# Revit family: VNRZ - 5.125'' 2-5-Door - All
name_source: partatom
category: Mechanical Equipment
units: mm (PartAtom-declared; Revit-internal decimal feet)

## family parameters
Always vertical = Yes
Cut with Voids When Loaded = No
OmniClass Number = 23.40.40.11.17
OmniClass Title = Refrigerated Cases
Part Type = Normal
Room Calculation Point = No
Round Connector Dimension = Use Diameter
Shared = Yes
Work Plane-Based = Yes

## types (5) — shared parameters
24" Shelf = Yes
DATE = 03-16-2015
DEFROST WATTAGE = 0 W
DESIGNERS NAME = SHIDDRAMESH
DISCHARGE AIR TEMP = 0 °F
Default Elevation = 48"
Defrosts Per Day_2 = 1
Description = VNRZ
Discharge Air Velocity (FPM) = 455
END PANEL = <By Category>
EQUIPMENT DESCRIPTION = VNRZ
EQUIPMENT MARK = VNRZ
Electric Defrost Fail-Safe = 46
Electric Defrost Termination Temp (°F) = 50
GLASS = Glass
GLASS CLAMP = <By Category>
Heated/Low E = Heated
Height = 83 7/8"
Hot Gas Defrost Fail-Safe = 24
Hot Gas Defrost Termination = 73° F
Item Description = VNRZ
Keynote = VNRZ
Legend Number = VNRZ
Manufacturer = HILL PHOENIX
Model = VNRZ
PAINTED METAL UPPER SHELF = <By Category>
PVC PIPE = <By Category>
Run-Off Time (Min) = 13 - 15
STAINLESS STEEL = GALVANIZED STEEL
Size of Door = 30"
Superheat Set Point @ Bulb (°F) = 3-5
URL = http://www.hillphoenix.com
Width = 37 1/8"
zero-valued in all types: Actual Weight, Load Mbh

## per-type parameters (varying)
- 2-Door - Frozen - Heated: Application Discipline=Frozen; BTUH Conventional=1091; BTUH Parallel=1071; CENTER LINE=30"; Combined Heated Rails Amps=1 A; Combined Heated Rails Watts=72 W; Combined Low E Rails Amps=0 A; Combined Low E Rails Watts=43 W; DOOR CONFIGURATION=MASTER DOOR : 30" X 75" 2 DOOR A SWING (LEFT OPENING); DRAIN HEATER AMPS=1 A; DRAIN HEATER WATTS=152 W; Defrost (Phase 1) 208 V Amps=7 A; Defrost (Phase 1) 208 V Watts=1552 W; Defrost (Phase 1) 240 V Amps=9 A; Defrost (Phase 1) 240 V Watts=2068 W; Discharge Air (°F)=-1; Eliminaator Amps=3 A; Eliminaator Watts=312 W; Evaporator (°F)=-7; GE Immersion Amps=0 A; GE Immersion Watts=37 W; High Efficiency Amps=1 A; High Efficiency Watts=52 W; Individual 101-LE Frame Amps=1 A; Individual 101-LE Frame Watts=163 W; Individual Heated Doors Amps=1 A; Individual Heated Doors Watts=79 W; Individual Low E Doors Amps=0 A; Individual Low E Doors Watts=45 W; Length=60"; Length of Cases=60"; No. OF DOORS=2; Number of Fans=2; Optimax Pro Amps=0 A; Optimax Pro Watts=43 W; REF PLANE LEFT RIGHT=30"; REFRIGERATION PIPING=COPPER PIPE; Tank/Drain Heater Amps=1 A; Tank/Drain Heater Watts=152 W; Trim colour=Render Material 255-255-255; Type of Door Swing=B-Swing; pannel colour=Render Material 255-127-0
- 3-Door - Frozen - Heated: Application Discipline=Frozen; BTUH Conventional=1037; BTUH Parallel=1017; CENTER LINE=45"; Combined Heated Rails Amps=1 A; Combined Heated Rails Watts=109 W; Combined Low E Rails Amps=1 A; Combined Low E Rails Watts=64 W; DOOR CONFIGURATION=MASTER DOOR : 30" X 75" 3 DOOR A SWING (LEFT OPENING); DRAIN HEATER AMPS=1 A; DRAIN HEATER WATTS=171 W; Defrost (Phase 1) 208 V Amps=11 A; Defrost (Phase 1) 208 V Watts=2274 W; Defrost (Phase 1) 240 V Amps=13 A; Defrost (Phase 1) 240 V Watts=3018 W; Discharge Air (°F)=-1; Eliminaator Amps=4 A; Eliminaator Watts=461 W; Evaporator (°F)=-7; GE Immersion Amps=0 A; GE Immersion Watts=55 W; High Efficiency Amps=1 A; High Efficiency Watts=78 W; Individual 101-LE Frame Amps=2 A; Individual 101-LE Frame Watts=228 W; Individual Heated Doors Amps=1 A; Individual Heated Doors Watts=118 W; Individual Low E Doors Amps=1 A; Individual Low E Doors Watts=67 W; Length=90"; Length of Cases=90"; No. OF DOORS=3; Number of Fans=3; Optimax Pro Amps=1 A; Optimax Pro Watts=65 W; REF PLANE LEFT RIGHT=45"; REFRIGERATION PIPING=<By Category>; Tank/Drain Heater Amps=1 A; Tank/Drain Heater Watts=171 W; Trim colour=<By Category>; Type of Door Swing=A-Swing; pannel colour=<By Category>
- 4-Door - Frozen - Heated: Application Discipline=Ice Cream; BTUH Conventional=1188; BTUH Parallel=1159; CENTER LINE=60"; Combined Heated Rails Amps=1 A; Combined Heated Rails Watts=145 W; Combined Low E Rails Amps=1 A; Combined Low E Rails Watts=85 W; DOOR CONFIGURATION=MASTER DOOR : 30" X 75" 4 DOOR A SWING (LEFT OPENING); DRAIN HEATER AMPS=2 A; DRAIN HEATER WATTS=227 W; Defrost (Phase 1) 208 V Amps=14 A; Defrost (Phase 1) 208 V Watts=2984 W; Defrost (Phase 1) 240 V Amps=17 A; Defrost (Phase 1) 240 V Watts=3992 W; Discharge Air (°F)=-8; Eliminaator Amps=5 A; Eliminaator Watts=613 W; Evaporator (°F)=-15; GE Immersion Amps=1 A; GE Immersion Watts=73 W; High Efficiency Amps=1 A; High Efficiency Watts=104 W; Individual 101-LE Frame Amps=2 A; Individual 101-LE Frame Watts=298 W; Individual Heated Doors Amps=1 A; Individual Heated Doors Watts=158 W; Individual Low E Doors Amps=1 A; Individual Low E Doors Watts=89 W; Length=120"; Length of Cases=120"; No. OF DOORS=4; Number of Fans=4; Optimax Pro Amps=1 A; Optimax Pro Watts=87 W; REF PLANE LEFT RIGHT=60"; REFRIGERATION PIPING=<By Category>; Tank/Drain Heater Amps=2 A; Tank/Drain Heater Watts=227 W; Trim colour=<By Category>; Type of Door Swing=B-Swing; pannel colour=<By Category>
- 5-Door - Frozen - Heated: Application Discipline=Ice Cream; BTUH Conventional=1129; BTUH Parallel=1101; CENTER LINE=75"; Combined Heated Rails Amps=2 A; Combined Heated Rails Watts=181 W; Combined Low E Rails Amps=1 A; Combined Low E Rails Watts=107 W; DOOR CONFIGURATION=MASTER DOOR : 30" X 75" 5 DOOR A SWING (LEFT OPENING); DRAIN HEATER AMPS=2 A; DRAIN HEATER WATTS=275 W; Defrost (Phase 1) 208 V Amps=18 A; Defrost (Phase 1) 208 V Watts=3640 W; Defrost (Phase 1) 240 V Amps=20 A; Defrost (Phase 1) 240 V Watts=4840 W; Discharge Air (°F)=-8; Eliminaator Amps=6 A; Eliminaator Watts=763 W; Evaporator (°F)=-15; GE Immersion Amps=1 A; GE Immersion Watts=91 W; High Efficiency Amps=2 A; High Efficiency Watts=130 W; Individual 101-LE Frame Amps=3 A; Individual 101-LE Frame Watts=360 W; Individual Heated Doors Amps=2 A; Individual Heated Doors Watts=197 W; Individual Low E Doors Amps=1 A; Individual Low E Doors Watts=112 W; Length=150"; Length of Cases=150"; No. OF DOORS=5; Number of Fans=5; Optimax Pro Amps=1 A; Optimax Pro Watts=109 W; REF PLANE LEFT RIGHT=75"; REFRIGERATION PIPING=<By Category>; Tank/Drain Heater Amps=2 A; Tank/Drain Heater Watts=275 W; Trim colour=<By Category>; Type of Door Swing=A-Swing; pannel colour=<By Category>
- 1-Door - Frozen - Heated: Application Discipline=Frozen; BTUH Conventional=1091; BTUH Parallel=1071; CENTER LINE=15 1/2"; Combined Heated Rails Amps=1 A; Combined Heated Rails Watts=72 W; Combined Low E Rails Amps=0 A; Combined Low E Rails Watts=43 W; DOOR CONFIGURATION=MASTER DOO1 : 30" X 75" 5 DOOR A SWING (LEFT OPENING); DRAIN HEATER AMPS=1 A; DRAIN HEATER WATTS=152 W; Defrost (Phase 1) 208 V Amps=7 A; Defrost (Phase 1) 208 V Watts=1552 W; Defrost (Phase 1) 240 V Amps=9 A; Defrost (Phase 1) 240 V Watts=2068 W; Discharge Air (°F)=-1; Eliminaator Amps=3 A; Eliminaator Watts=312 W; Evaporator (°F)=-7; GE Immersion Amps=0 A; GE Immersion Watts=37 W; High Efficiency Amps=1 A; High Efficiency Watts=52 W; Individual 101-LE Frame Amps=1 A; Individual 101-LE Frame Watts=163 W; Individual Heated Doors Amps=1 A; Individual Heated Doors Watts=79 W; Individual Low E Doors Amps=0 A; Individual Low E Doors Watts=45 W; Length=31"; Length of Cases=60"; No. OF DOORS=2; Number of Fans=2; Optimax Pro Amps=0 A; Optimax Pro Watts=43 W; REF PLANE LEFT RIGHT=15 1/2"; REFRIGERATION PIPING=COPPER PIPE; Tank/Drain Heater Amps=1 A; Tank/Drain Heater Watts=152 W; Trim colour=Render Material 255-255-255; Type of Door Swing=B-Swing; pannel colour=Render Material 255-127-0

## geometry (parser evidence)
native form markers: Blend x8, Sweep x19
no freeform markers — native parametric forms only
